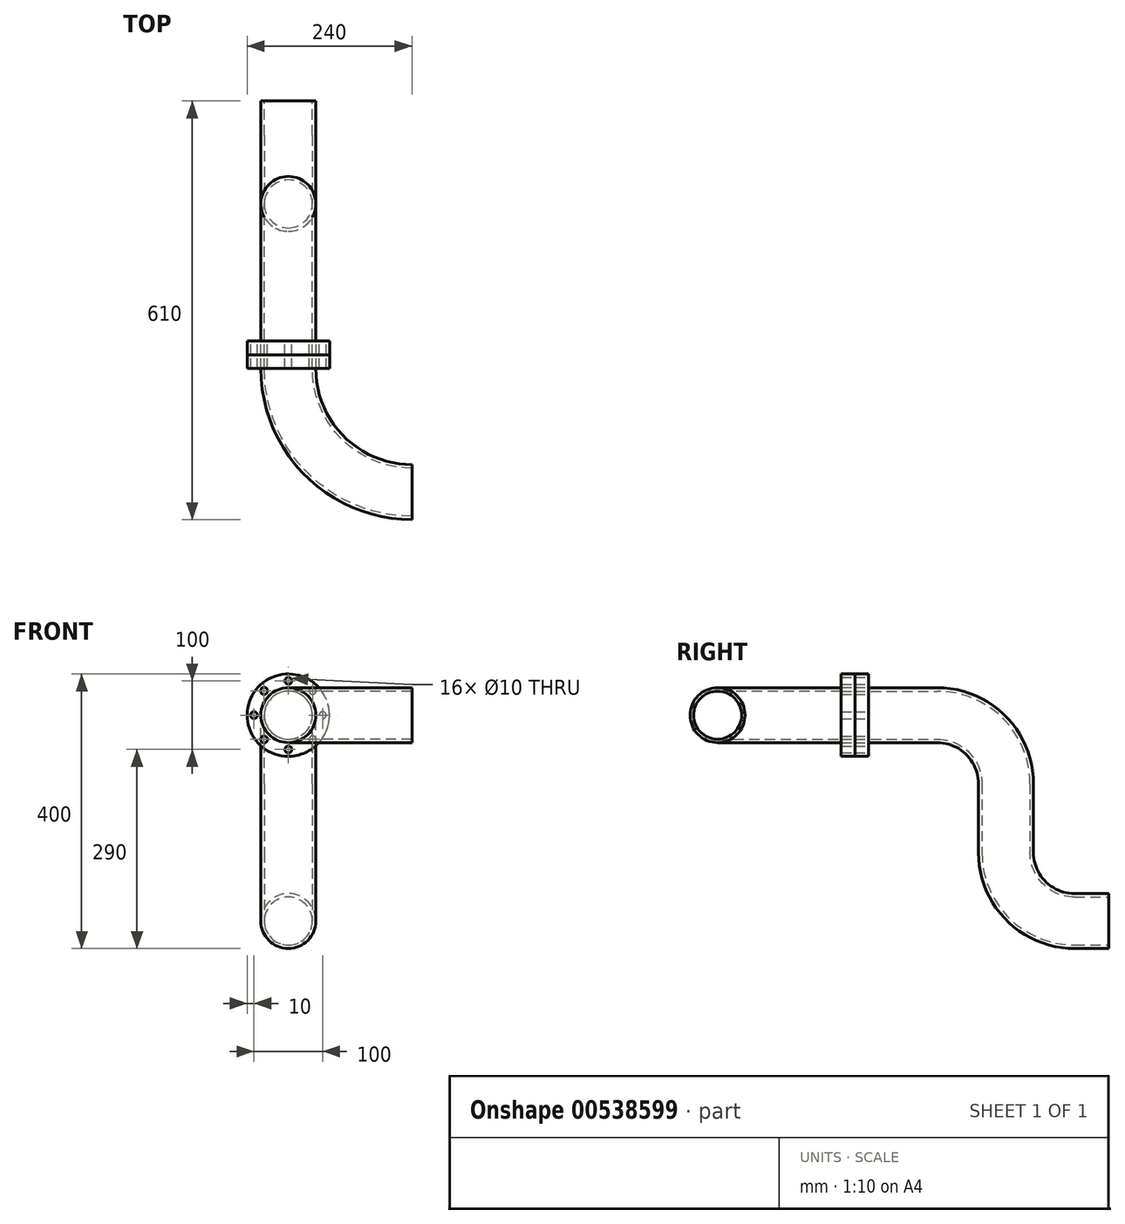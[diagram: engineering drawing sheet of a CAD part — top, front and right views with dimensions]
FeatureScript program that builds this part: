
annotation { "Feature Type Name" : "Feature", "Feature Type Description" : "" }
export const myFeature = defineFeature(function(context is Context, id is Id, definition is map)
    precondition{}
    {
        {
            var Q0;
            Q0=qCreatedBy(makeId("Front.planeOp"),FACE);
            var sketch = newSketch(context, id + "F0", { "sketchPlane" : qUnion([Q0])});
            skCircle(sketch, "E0", {"center": v(0, 0) * mm, "radius": 60 * mm});
            skCircle(sketch, "E1", {"center": v(0, 50) * mm, "radius": 5 * mm});
            skLineSegment(sketch, "E2", {"start": v(0, 0) * mm, "end": v(0, 50) * mm});
            skCircle(sketch, "E3.1.0", {"center": v(-35.36, 35.36) * mm, "radius": 5 * mm});
            skCircle(sketch, "E3.2.0", {"center": v(-50, 0) * mm, "radius": 5 * mm});
            skCircle(sketch, "E3.3.0", {"center": v(-35.36, -35.36) * mm, "radius": 5 * mm});
            skCircle(sketch, "E3.4.0", {"center": v(0, -50) * mm, "radius": 5 * mm});
            skCircle(sketch, "E3.5.0", {"center": v(35.36, -35.36) * mm, "radius": 5 * mm});
            skCircle(sketch, "E3.6.0", {"center": v(50, 0) * mm, "radius": 5 * mm});
            skCircle(sketch, "E3.7.0", {"center": v(35.36, 35.36) * mm, "radius": 5 * mm});
            skCircle(sketch, "E4", {"center": v(0, 0) * mm, "radius": 35 * mm});
            skSolve(sketch);
        }
        {
            var Q0;
            Q0=makeQuery(id+"F0.imprint","IMPRINT",FACE,{"disambiguationData":[TD([[makeQuery(id+"F0.imprint","IMPRINT",EDGE,{"derivedFrom":sQuery(id+"F0.wireOp",EDGE,"E0")}),1.0]])]});
            extrude(context, id + "F1", {"entities" : qUnion([Q0]), "depth" : 20 * mm, "offsetDistance" : 25 * mm});
        }
        {
            var Q0;
            Q0=qCreatedBy(makeId("Front.planeOp"),FACE);
            var sketch = newSketch(context, id + "F2", { "sketchPlane" : qUnion([Q0])});
            skCircle(sketch, "E5", {"center": v(0, 0) * mm, "radius": 35 * mm});
            skCircle(sketch, "E6", {"center": v(0, 0) * mm, "radius": 40 * mm});
            skSolve(sketch);
        }
        {
            var Q0;
            Q0=qCreatedBy(makeId("Right.planeOp"),FACE);
            var sketch = newSketch(context, id + "F3", { "sketchPlane" : qUnion([Q0])});
            skLineSegment(sketch, "E7", {"start": v(0, 0) * mm, "end": v(100, 0) * mm});
            skLineSegment(sketch, "E8", {"start": v(200, -100) * mm, "end": v(200, -200) * mm});
            skLineSegment(sketch, "E9", {"start": v(300, -300) * mm, "end": v(350, -300) * mm});
            skPoint(sketch, "E10.visualSharp", {"position": v(200, 0) * mm});
            skArc(sketch, "E10.filletArc", {"start": v(200, -100) * mm, "mid": v(170.71, -29.29) * mm, "end": v(100, 0) * mm});
            skPoint(sketch, "E11.visualSharp", {"position": v(200, -300) * mm});
            skArc(sketch, "E11.filletArc", {"start": v(200, -200) * mm, "mid": v(229.29, -270.71) * mm, "end": v(300, -300) * mm});
            skSolve(sketch);
        }
        {
            var Q0;
            Q0=makeQuery(id+"F2.imprint","IMPRINT",FACE,{"disambiguationData":[TD([[makeQuery(id+"F2.imprint","IMPRINT",EDGE,{"derivedFrom":sQuery(id+"F2.wireOp",EDGE,"E5")}),-1.0]])]});
            var Q1;
            Q1=sQuery(id+"F3.wireOp",EDGE,"E11.filletArc");
            var Q2;
            Q2=sQuery(id+"F3.wireOp",EDGE,"E8");
            var Q3;
            Q3=sQuery(id+"F3.wireOp",EDGE,"E10.filletArc");
            var Q4;
            Q4=sQuery(id+"F3.wireOp",EDGE,"E7");
            var Q5;
            Q5=sQuery(id+"F3.wireOp",EDGE,"E9");
            sweep(context, id + "F4", {"operationType" : NewBodyOperationType.ADD, "profiles" : qUnion([Q0]), "path" : qUnion([Q1, Q2, Q3, Q4, Q5])});
        }
        {
            var Q0;
            Q0=makeQuery(id+"F1.opExtrude","CAP_FACE",FACE,{"disambiguationData":[OSD([sQuery(id+"F0.wireOp",EDGE,"E0"),sQuery(id+"F0.wireOp",EDGE,"E1"),sQuery(id+"F0.wireOp",EDGE,"E3.1.0"),sQuery(id+"F0.wireOp",EDGE,"E3.2.0"),sQuery(id+"F0.wireOp",EDGE,"E3.3.0"),sQuery(id+"F0.wireOp",EDGE,"E3.4.0"),sQuery(id+"F0.wireOp",EDGE,"E3.5.0"),sQuery(id+"F0.wireOp",EDGE,"E3.6.0"),sQuery(id+"F0.wireOp",EDGE,"E3.7.0"),sQuery(id+"F0.wireOp",EDGE,"E4")])],"isStart":false});
            extrude(context, id + "F5", {"entities" : qUnion([Q0]), "depth" : 20 * mm, "offsetDistance" : 25 * mm});
        }
        {
            var Q0;
            Q0=makeQuery(id+"F5.opExtrude","CAP_FACE",FACE,{"disambiguationData":[OSD([sQuery(id+"F0.wireOp",EDGE,"E0"),sQuery(id+"F0.wireOp",EDGE,"E1"),sQuery(id+"F0.wireOp",EDGE,"E3.1.0"),sQuery(id+"F0.wireOp",EDGE,"E3.2.0"),sQuery(id+"F0.wireOp",EDGE,"E3.3.0"),sQuery(id+"F0.wireOp",EDGE,"E3.4.0"),sQuery(id+"F0.wireOp",EDGE,"E3.5.0"),sQuery(id+"F0.wireOp",EDGE,"E3.6.0"),sQuery(id+"F0.wireOp",EDGE,"E3.7.0"),sQuery(id+"F0.wireOp",EDGE,"E4")])],"isStart":false});
            var sketch = newSketch(context, id + "F6", { "sketchPlane" : qUnion([Q0])});
            skCircle(sketch, "E12", {"center": v(0, 0) * mm, "radius": 35 * mm});
            skCircle(sketch, "E13", {"center": v(0, 0) * mm, "radius": 40 * mm});
            skLineSegment(sketch, "E14", {"start": v(0, 0) * mm, "end": v(180, 0) * mm, "construction": true});
            skLineSegment(sketch, "E15", {"start": v(180, 87.5) * mm, "end": v(180, -111.76) * mm, "construction": true});
            skSolve(sketch);
        }
        {
            var Q0;
            Q0=makeQuery(id+"F6.imprint","IMPRINT",FACE,{"disambiguationData":[TD([[makeQuery(id+"F6.imprint","IMPRINT",EDGE,{"derivedFrom":sQuery(id+"F6.wireOp",EDGE,"E12")}),-1.0]])]});
            var Q1;
            Q1=sQuery(id+"F6.wireOp",EDGE,"E15");
            revolve(context, id + "F7", {"operationType" : NewBodyOperationType.ADD, "entities" : qUnion([Q0]), "axis" : qUnion([Q1]), "revolveType" : RevolveType.ONE_DIRECTION, "oppositeDirection" : true, "angle" : 90 * degree});
        }
    });
